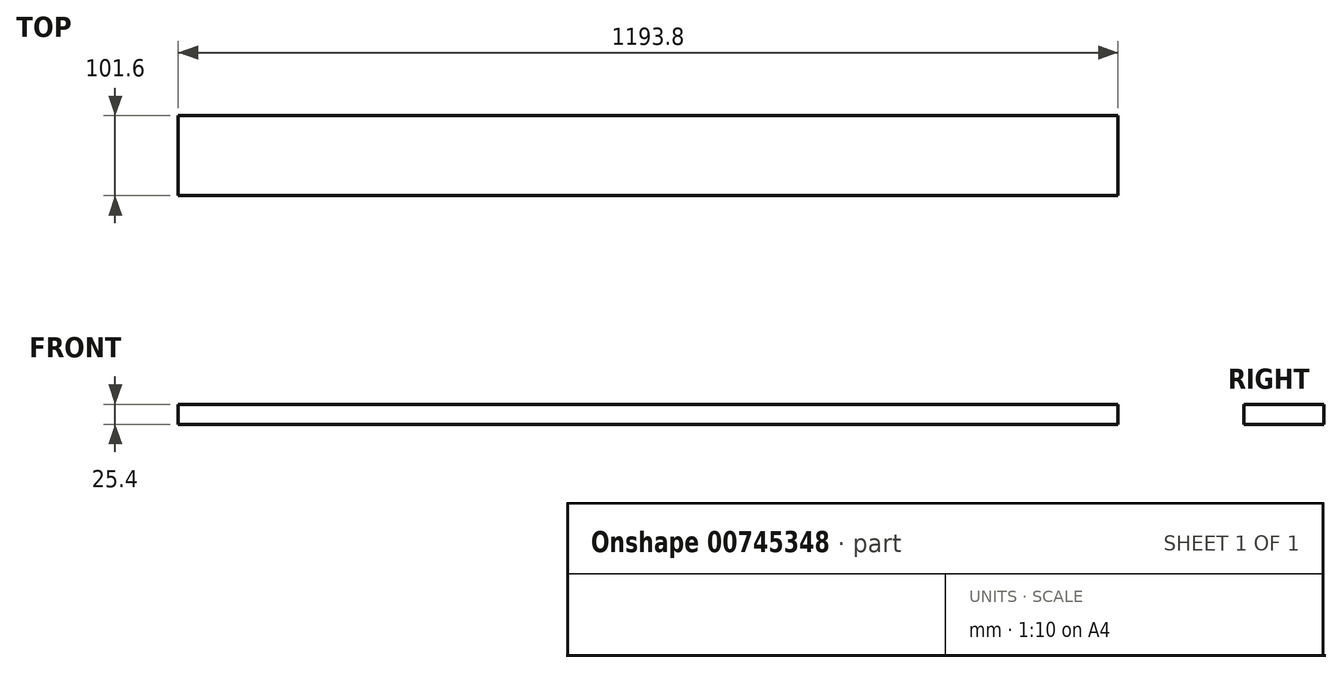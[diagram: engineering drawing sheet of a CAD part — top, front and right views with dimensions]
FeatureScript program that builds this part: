
annotation { "Feature Type Name" : "Feature", "Feature Type Description" : "" }
export const myFeature = defineFeature(function(context is Context, id is Id, definition is map)
    precondition{}
    {
        {
            var Q0;
            Q0=qCreatedBy(makeId("Top.planeOp"),FACE);
            var sketch = newSketch(context, id + "F0", { "sketchPlane" : qUnion([Q0])});
            skLineSegment(sketch, "E0.bottom", {"start": v(0, 0) * mm, "end": v(1193.8, 0) * mm});
            skLineSegment(sketch, "E0.top", {"start": v(0, 101.6) * mm, "end": v(1193.8, 101.6) * mm});
            skLineSegment(sketch, "E0.left", {"start": v(0, 0) * mm, "end": v(0, 101.6) * mm});
            skLineSegment(sketch, "E0.right", {"start": v(1193.8, 0) * mm, "end": v(1193.8, 101.6) * mm});
            skSolve(sketch);
        }
        {
            var Q0;
            Q0=makeQuery(id+"F0.imprint","IMPRINT",FACE,{"disambiguationData":[TD([[makeQuery(id+"F0.imprint","IMPRINT",EDGE,{"derivedFrom":sQuery(id+"F0.wireOp",EDGE,"E0.bottom")}),1.0]])]});
            extrude(context, id + "F1", {"entities" : qUnion([Q0]), "depth" : 25.4 * mm, "offsetDistance" : 25.4 * mm});
        }
    });
